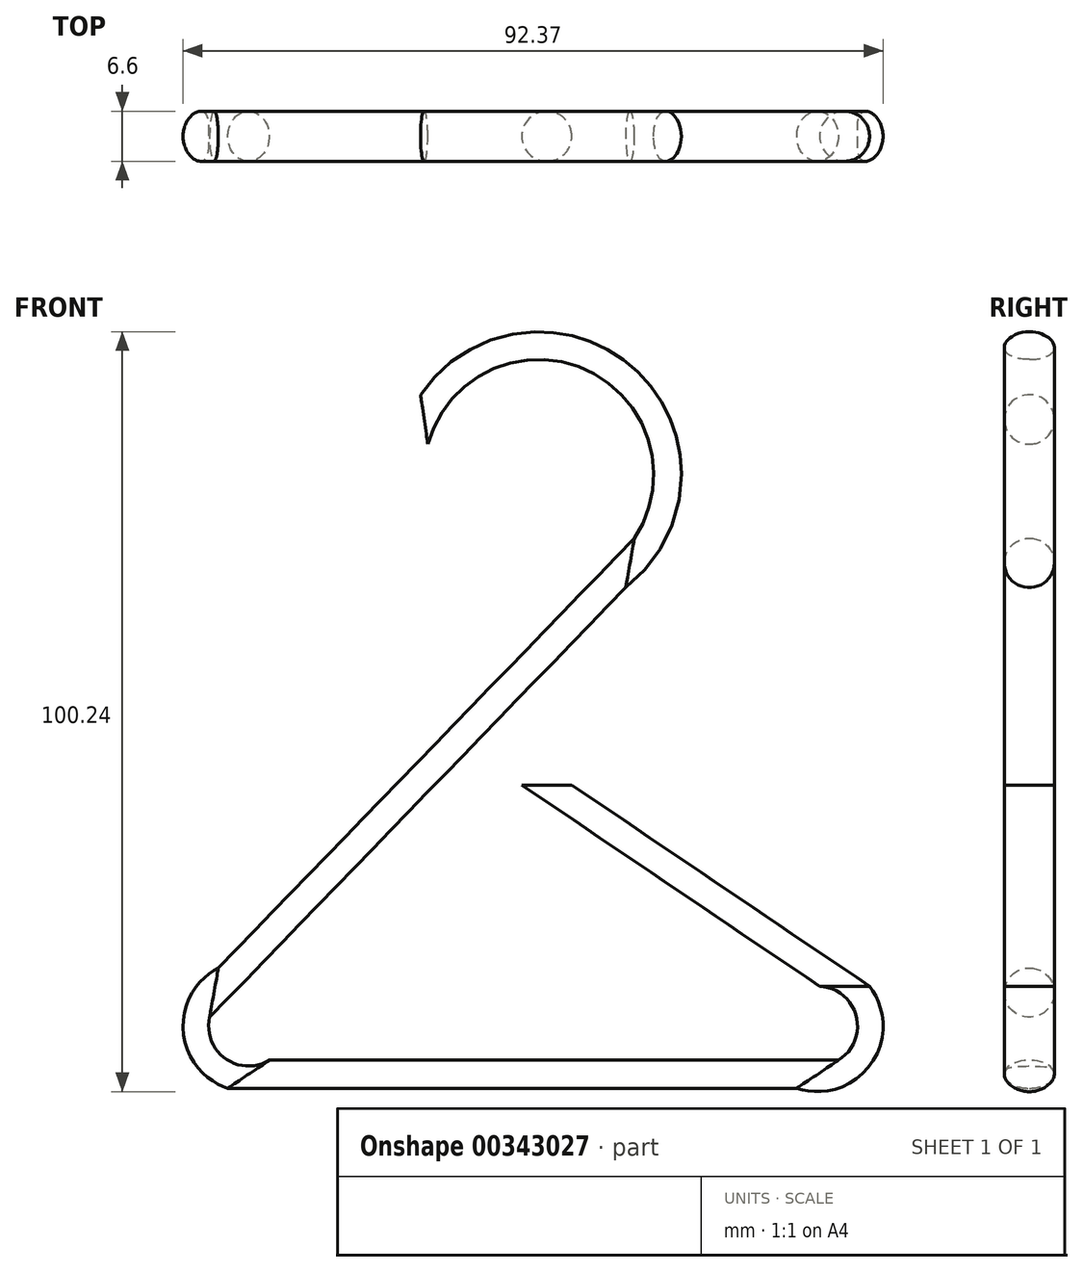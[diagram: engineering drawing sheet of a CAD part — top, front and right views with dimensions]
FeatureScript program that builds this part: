
annotation { "Feature Type Name" : "Feature", "Feature Type Description" : "" }
export const myFeature = defineFeature(function(context is Context, id is Id, definition is map)
    precondition{}
    {
        {
            var Q0;
            Q0=qCreatedBy(makeId("Front.planeOp"),FACE);
            var sketch = newSketch(context, id + "F0", { "sketchPlane" : qUnion([Q0])});
            skLineSegment(sketch, "E0", {"start": v(0, 0) * mm, "end": v(39.29, -26.55) * mm});
            skLineSegment(sketch, "E1", {"start": v(35.73, -38.16) * mm, "end": v(-39.35, -38.16) * mm});
            skLineSegment(sketch, "E2", {"start": v(-43.91, -27.4) * mm, "end": v(10.99, 29.3) * mm});
            skPoint(sketch, "E3.visualSharp", {"position": v(56.47, -38.16) * mm});
            skArc(sketch, "E3.filletArc", {"start": v(35.73, -38.16) * mm, "mid": v(41.8, -33.67) * mm, "end": v(39.29, -26.55) * mm});
            skPoint(sketch, "E4.visualSharp", {"position": v(-54.34, -38.16) * mm});
            skArc(sketch, "E4.filletArc", {"start": v(-43.91, -27.4) * mm, "mid": v(-45.2, -34.29) * mm, "end": v(-39.35, -38.16) * mm});
            skArc(sketch, "E5", {"start": v(10.99, 29.3) * mm, "mid": v(8.53, 54.74) * mm, "end": v(-16.18, 48.23) * mm});
            skSolve(sketch);
        }
        {
            var Q0;
            Q0=qCreatedBy(makeId("Top.planeOp"),FACE);
            var sketch = newSketch(context, id + "F1", { "sketchPlane" : qUnion([Q0])});
            skCircle(sketch, "E6", {"center": v(0, 0) * mm, "radius": 3.3 * mm});
            skSolve(sketch);
        }
        {
            var Q0;
            Q0=makeQuery(id+"F1.imprint","IMPRINT",FACE,{"disambiguationData":[TD([[makeQuery(id+"F1.imprint","IMPRINT",EDGE,{"derivedFrom":sQuery(id+"F1.wireOp",EDGE,"E6")}),1.0]])]});
            var Q1;
            Q1 = qConstructionFilter(qBodyType(qCreatedBy(id + "F0" ,EDGE), BodyType.WIRE), ConstructionObject.NO);
            sweep(context, id + "F2", {"profiles" : qUnion([Q0]), "path" : qUnion([Q1])});
        }
    });
